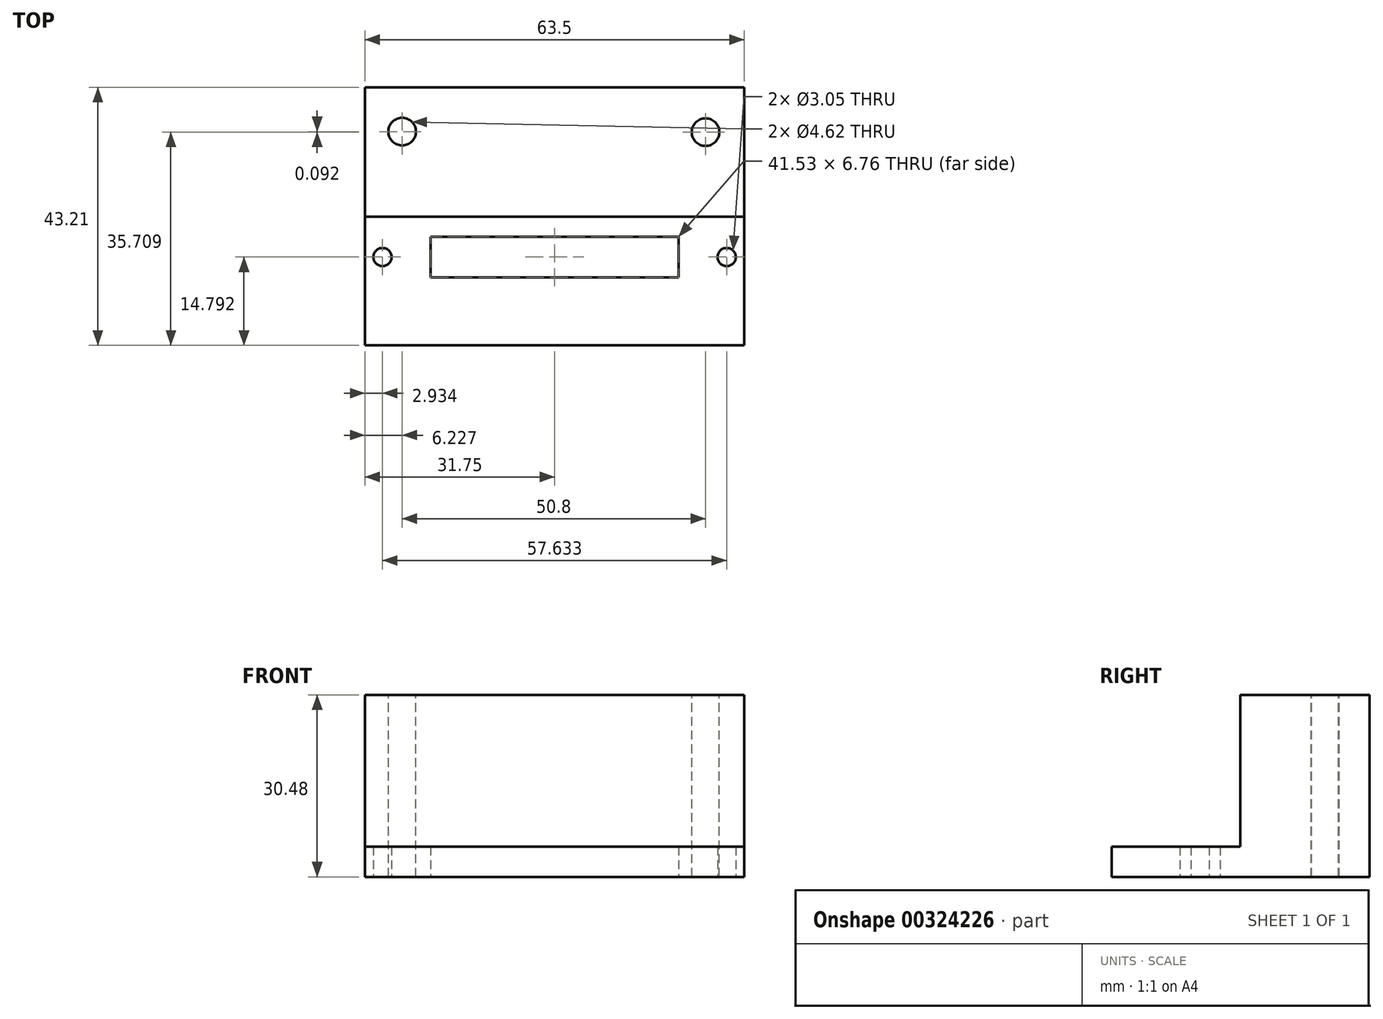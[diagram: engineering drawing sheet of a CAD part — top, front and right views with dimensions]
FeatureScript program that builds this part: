
annotation { "Feature Type Name" : "Feature", "Feature Type Description" : "" }
export const myFeature = defineFeature(function(context is Context, id is Id, definition is map)
    precondition{}
    {
        {
            var Q0;
            Q0=qCreatedBy(makeId("Top.planeOp"),FACE);
            var sketch = newSketch(context, id + "F0", { "sketchPlane" : qUnion([Q0])});
            skLineSegment(sketch, "E0.bottom", {"start": v(0, 0) * mm, "end": v(63.5, 0) * mm});
            skLineSegment(sketch, "E0.top", {"start": v(0, 30.51) * mm, "end": v(63.5, 30.51) * mm});
            skLineSegment(sketch, "E0.left", {"start": v(0, 0) * mm, "end": v(0, 30.51) * mm});
            skLineSegment(sketch, "E0.right", {"start": v(63.5, 0) * mm, "end": v(63.5, 30.51) * mm});
            skLineSegment(sketch, "E1.bottom", {"start": v(10.99, 18.17) * mm, "end": v(52.51, 18.17) * mm});
            skLineSegment(sketch, "E1.top", {"start": v(10.99, 11.41) * mm, "end": v(52.51, 11.41) * mm});
            skLineSegment(sketch, "E1.left", {"start": v(10.99, 18.17) * mm, "end": v(10.99, 11.41) * mm});
            skLineSegment(sketch, "E1.right", {"start": v(52.51, 18.17) * mm, "end": v(52.51, 11.41) * mm});
            skCircle(sketch, "E2", {"center": v(60.57, 14.8) * mm, "radius": 1.52 * mm});
            skCircle(sketch, "E3", {"center": v(2.93, 14.8) * mm, "radius": 1.52 * mm});
            skPoint(sketch, "E4", {"position": v(10.99, 14.8) * mm});
            skPoint(sketch, "E5", {"position": v(31.75, 18.17) * mm});
            skPoint(sketch, "E6", {"position": v(31.75, 30.51) * mm});
            skSolve(sketch);
        }
        {
            var Q0;
            Q0=makeQuery(id+"F0.imprint","IMPRINT",FACE,{"disambiguationData":[TD([[makeQuery(id+"F0.imprint","IMPRINT",EDGE,{"derivedFrom":sQuery(id+"F0.wireOp",EDGE,"E0.bottom")}),1.0]])]});
            extrude(context, id + "F1", {"entities" : qUnion([Q0]), "depth" : 5.08 * mm});
        }
        {
            var Q0;
            Q0=makeQuery(id+"F1.opExtrude","CAP_FACE",FACE,{"disambiguationData":[OSD([sQuery(id+"F0.wireOp",EDGE,"E0.bottom"),sQuery(id+"F0.wireOp",EDGE,"E0.top"),sQuery(id+"F0.wireOp",EDGE,"E0.left"),sQuery(id+"F0.wireOp",EDGE,"E0.right"),sQuery(id+"F0.wireOp",EDGE,"E1.bottom"),sQuery(id+"F0.wireOp",EDGE,"E1.top"),sQuery(id+"F0.wireOp",EDGE,"E1.left"),sQuery(id+"F0.wireOp",EDGE,"E1.right"),sQuery(id+"F0.wireOp",EDGE,"E2"),sQuery(id+"F0.wireOp",EDGE,"E3")])],"isStart":false});
            var sketch = newSketch(context, id + "F2", { "sketchPlane" : qUnion([Q0])});
            skLineSegment(sketch, "E7.bottom", {"start": v(0, 30.51) * mm, "end": v(63.5, 30.51) * mm});
            skLineSegment(sketch, "E7.top", {"start": v(0, 21.55) * mm, "end": v(63.5, 21.55) * mm});
            skLineSegment(sketch, "E7.left", {"start": v(0, 30.51) * mm, "end": v(0, 21.55) * mm});
            skLineSegment(sketch, "E7.right", {"start": v(63.5, 30.51) * mm, "end": v(63.5, 21.55) * mm});
            skSolve(sketch);
        }
        {
            var Q0;
            Q0=makeQuery(id+"F2.imprint","IMPRINT",FACE,{"disambiguationData":[TD([[makeQuery(id+"F2.imprint","IMPRINT",EDGE,{"derivedFrom":sQuery(id+"F2.wireOp",EDGE,"E7.bottom")}),-1.0]])]});
            extrude(context, id + "F3", {"entities" : qUnion([Q0]), "operationType" : NewBodyOperationType.ADD, "depth" : 25.4 * mm});
        }
        {
            var Q0;
            Q0=makeQuery(id+"F3.boolean.opBoolean","MERGE",FACE,{"derivedFrom":[makeQuery(id+"F1.opExtrude","SWEPT_FACE",FACE,{"disambiguationData":[OSD([sQuery(id+"F0.wireOp",EDGE,"E0.top")])]}),makeQuery(id+"F3.opExtrude","SWEPT_FACE",FACE,{"disambiguationData":[OSD([sQuery(id+"F2.wireOp",EDGE,"E7.bottom")])]})]});
            var sketch = newSketch(context, id + "F4", { "sketchPlane" : qUnion([Q0])});
            skLineSegment(sketch, "E8.bottom", {"start": v(-63.5, 30.48) * mm, "end": v(0, 30.48) * mm});
            skLineSegment(sketch, "E8.top", {"start": v(-63.5, 21.97) * mm, "end": v(0, 21.97) * mm});
            skLineSegment(sketch, "E8.left", {"start": v(-63.5, 30.48) * mm, "end": v(-63.5, 21.97) * mm});
            skLineSegment(sketch, "E8.right", {"start": v(0, 30.48) * mm, "end": v(0, 21.97) * mm});
            skSolve(sketch);
        }
        {
            var Q0;
            Q0=makeQuery(id+"F4.imprint","IMPRINT",FACE,{"disambiguationData":[TD([[makeQuery(id+"F4.imprint","IMPRINT",EDGE,{"derivedFrom":sQuery(id+"F4.wireOp",EDGE,"E8.bottom")}),1.0]])]});
            extrude(context, id + "F5", {"entities" : qUnion([Q0]), "operationType" : NewBodyOperationType.ADD, "depth" : 12.7 * mm});
        }
        {
            var Q0;
            Q0=makeQuery(id+"F5.boolean.opBoolean","MERGE",FACE,{"derivedFrom":[makeQuery(id+"F3.opExtrude","CAP_FACE",FACE,{"disambiguationData":[OSD([sQuery(id+"F2.wireOp",EDGE,"E7.bottom"),sQuery(id+"F2.wireOp",EDGE,"E7.top"),sQuery(id+"F2.wireOp",EDGE,"E7.left"),sQuery(id+"F2.wireOp",EDGE,"E7.right")])],"isStart":false}),makeQuery(id+"F5.opExtrude","SWEPT_FACE",FACE,{"disambiguationData":[OSD([sQuery(id+"F4.wireOp",EDGE,"E8.bottom")])]})]});
            var sketch = newSketch(context, id + "F6", { "sketchPlane" : qUnion([Q0])});
            skCircle(sketch, "E9", {"center": v(57.03, 35.7) * mm, "radius": 2.31 * mm});
            skCircle(sketch, "E10", {"center": v(6.23, 35.8) * mm, "radius": 2.31 * mm});
            skSolve(sketch);
        }
        {
            var Q0;
            Q0=makeQuery(id+"F6.imprint","IMPRINT",FACE,{"disambiguationData":[TD([[makeQuery(id+"F6.imprint","IMPRINT",EDGE,{"derivedFrom":sQuery(id+"F6.wireOp",EDGE,"E9")}),1.0]])]});
            var Q1;
            Q1=makeQuery(id+"F6.imprint","IMPRINT",FACE,{"disambiguationData":[TD([[makeQuery(id+"F6.imprint","IMPRINT",EDGE,{"derivedFrom":sQuery(id+"F6.wireOp",EDGE,"E10")}),1.0]])]});
            extrude(context, id + "F7", {"entities" : qUnion([Q0, Q1]), "operationType" : NewBodyOperationType.REMOVE, "oppositeDirection" : true, "depth" : 25.4 * mm});
        }
        {
            var Q0;
            Q0=makeQuery(id+"F5.opExtrude","SWEPT_FACE",FACE,{"disambiguationData":[OSD([sQuery(id+"F4.wireOp",EDGE,"E8.top")])]});
            var Q1;
            Q1=makeQuery(id+"F1.opExtrude","CAP_FACE",FACE,{"disambiguationData":[OSD([sQuery(id+"F0.wireOp",EDGE,"E0.bottom"),sQuery(id+"F0.wireOp",EDGE,"E0.top"),sQuery(id+"F0.wireOp",EDGE,"E0.left"),sQuery(id+"F0.wireOp",EDGE,"E0.right"),sQuery(id+"F0.wireOp",EDGE,"E1.bottom"),sQuery(id+"F0.wireOp",EDGE,"E1.top"),sQuery(id+"F0.wireOp",EDGE,"E1.left"),sQuery(id+"F0.wireOp",EDGE,"E1.right"),sQuery(id+"F0.wireOp",EDGE,"E2"),sQuery(id+"F0.wireOp",EDGE,"E3")])],"isStart":true});
            var Q2;
            Q2=makeQuery(id+"F1.opExtrude","SWEPT_BODY",BODY,{"disambiguationData":[OSD([sQuery(id+"F0.wireOp",EDGE,"E0.bottom"),sQuery(id+"F0.wireOp",EDGE,"E0.top"),sQuery(id+"F0.wireOp",EDGE,"E0.left"),sQuery(id+"F0.wireOp",EDGE,"E0.right"),sQuery(id+"F0.wireOp",EDGE,"E1.bottom"),sQuery(id+"F0.wireOp",EDGE,"E1.top"),sQuery(id+"F0.wireOp",EDGE,"E1.left"),sQuery(id+"F0.wireOp",EDGE,"E1.right"),sQuery(id+"F0.wireOp",EDGE,"E2"),sQuery(id+"F0.wireOp",EDGE,"E3")])]});
            extrude(context, id + "F8", {"entities" : qUnion([Q0]), "operationType" : NewBodyOperationType.ADD, "endBound" : BoundingType.UP_TO_SURFACE, "endBoundEntityFace" : qUnion([Q1]), "endBoundEntityBody" : qUnion([Q2]), "depth" : 20.32 * mm});
        }
    });
